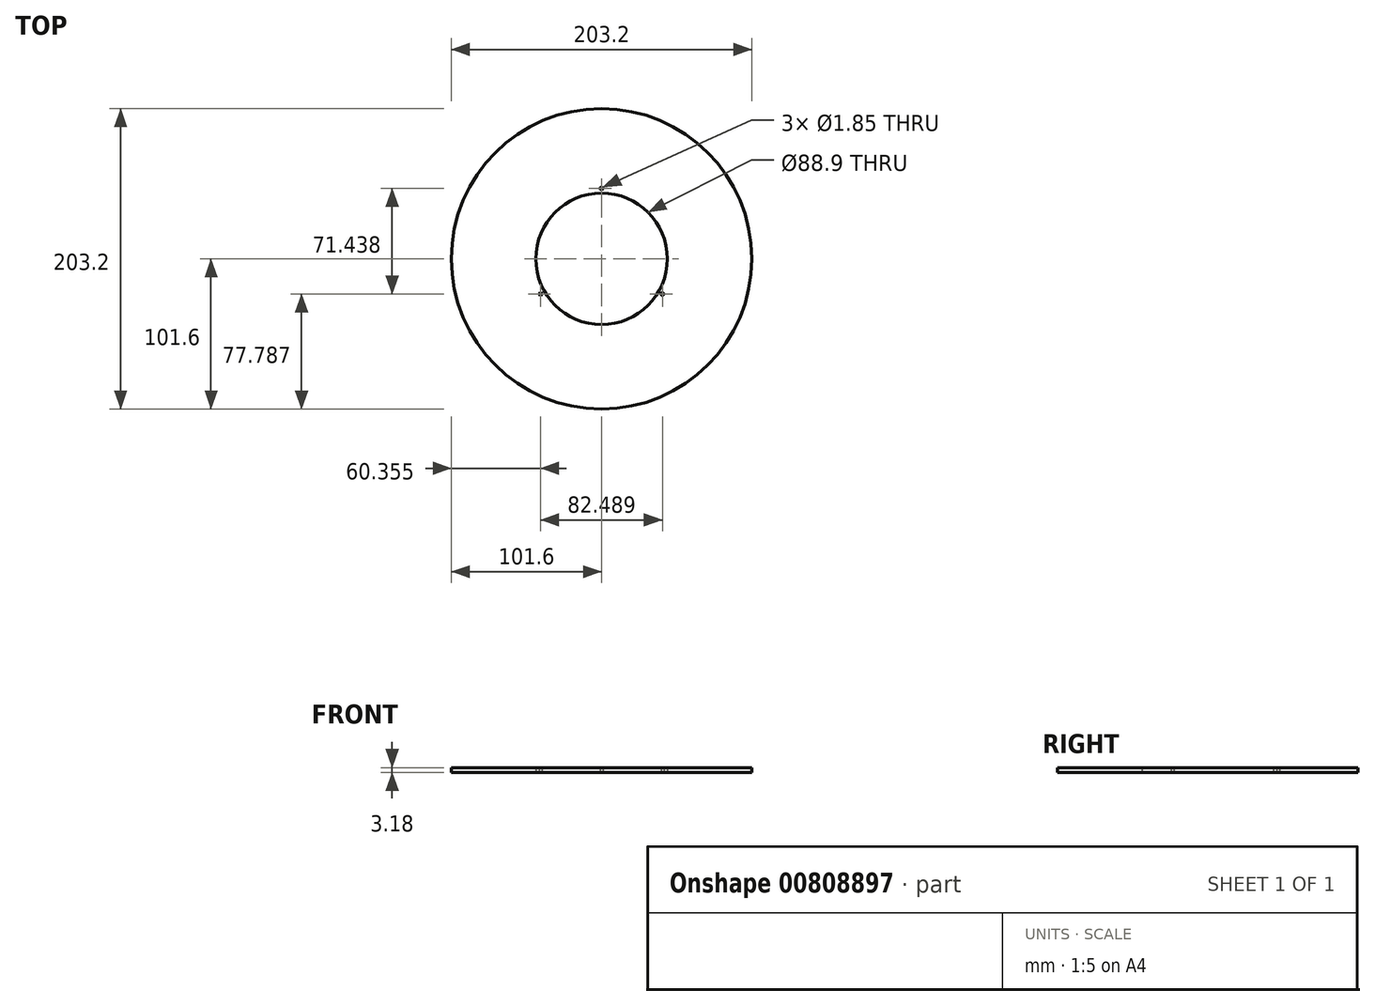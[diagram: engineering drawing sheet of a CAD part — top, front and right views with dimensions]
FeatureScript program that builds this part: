
annotation { "Feature Type Name" : "Feature", "Feature Type Description" : "" }
export const myFeature = defineFeature(function(context is Context, id is Id, definition is map)
    precondition{}
    {
        {
            var Q0;
            Q0=qCreatedBy(makeId("Top.planeOp"),FACE);
            var sketch = newSketch(context, id + "F0", { "sketchPlane" : qUnion([Q0])});
            skCircle(sketch, "E0", {"center": v(0, 0) * mm, "radius": 101.6 * mm});
            skCircle(sketch, "E1", {"center": v(0, 0) * mm, "radius": 44.45 * mm});
            skCircle(sketch, "E2", {"center": v(0, 47.63) * mm, "radius": 0.93 * mm});
            skCircle(sketch, "E3", {"center": v(41.24, -23.81) * mm, "radius": 0.93 * mm});
            skCircle(sketch, "E4", {"center": v(-41.24, -23.81) * mm, "radius": 0.93 * mm});
            skSolve(sketch);
        }
        {
            var Q0;
            Q0=makeQuery(id+"F0.imprint","IMPRINT",FACE,{"disambiguationData":[TD([[makeQuery(id+"F0.imprint","IMPRINT",EDGE,{"derivedFrom":sQuery(id+"F0.wireOp",EDGE,"E0")}),1.0]])]});
            extrude(context, id + "F1", {"entities" : qUnion([Q0]), "depth" : 3.17 * mm, "offsetDistance" : 25.4 * mm});
        }
    });
